# Revit family: 23  MAGIC SUSPENDED LED LINEAR LIGHT
name_source: partatom
category: Lighting Fixtures
units: mm (PartAtom-declared; Revit-internal decimal feet)

## family parameters
Cut with Voids When Loaded = No
Host = Face
Light Source = Yes
Part Type = Normal
Room Calculation Point = No
Round Connector Dimension = Use Diameter
Shared = No

## types (6) — shared parameters
Apparent Load = 0 VA
Average life based on 77F(HRS) = 50000
CRI = 80
Color Filter = 16777215
Default Elevation = 0' - 0"
Description = This MAGIC led linear fixture is a 2.3 wide linear architectural luminaire with a slim and discreet profile
Dimming / Control = 0-10 V
Dimming Lamp Color Temperature Shift = <None>
Finish/Color = White Aluminum
IP Rating = 20
Inside Element = white inside
Load Classification = Lighting
Manufacturer = Above All Lighting
Power Factor = 1
Type Comments = 2.3 MAGIC SUSPENDED LED LINEAR LIGHT Direct and Indirect Light
URL = https://www.abovealllighting.com
Voltage = 120-277 V

## per-type parameters (varying)
| type | B | Fixture Length | Order number | PSM | Photometric Web File | Suspender Height | Tilt Angle | Wall Mount | Wattage Comments |
| MAG2423-SW1-PSM-SD-FDL | 3' - 6 11/32" | 7' - 10 11/16" | 16682 | Yes | MAG2423_FDL_4000K_UP10_DOWN90.IES | 4' - 0" | -90.00° | No | 40W/60W/80W |
| MAG1223-SW1-PSM-SD-FDL | 1' - 6 23/32" | 3' - 11 7/16" | 16265 | Yes | MAG1223-FDL-WH (4000K, DOWN100%).IES | 4' - 0" | -90.00° | No | 20W/30W/40W |
| MAG0623-SW1-PSM-SD-FDL | 0' - 6 29/32" | 1' - 11 13/16" | 17009 | Yes | MAG0623-FDL-WH (4000K, DOWN100%).IES | 4' - 0" | -90.00° | No | 10W/15W/20W |
| MAG2423-SW1-WM-SD-FDL | 3' - 6 11/32" | 7' - 10 11/16" | 17009 | No | MAG2423_FDL_4000K_UP10_DOWN90.IES | 0' - 4" | -90.00° | Yes | 40W/60W/80W |
| MAG1223-SW1-WM-SD-FDL | 1' - 6 23/32" | 3' - 11 7/16" | 17010 | No | MAG1223-FDL-WH (4000K, DOWN100%).IES | 0' - 4" | -90.00° | Yes | 20W/30W/40W |
| MAG0623-SW1-WM-SD-FDL | 0' - 6 29/32" | 1' - 11 13/16" | 17011 | No | MAG0623-FDL-WH (4000K, DOWN100%).IES | 0' - 4" | 90.00° | Yes | 10W/15W/20W |

note: column(s) folded — value = type name in every type: Model

## geometry (parser evidence)
native form markers: Sweep x8
no freeform markers — native parametric forms only
